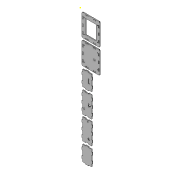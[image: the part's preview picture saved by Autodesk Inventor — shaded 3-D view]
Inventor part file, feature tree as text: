
AUTODESK INVENTOR PART (.ipt)
format: ipt  version: 2022 (Build 260153000, 153)  size: 1,122,816 bytes
history: native  units: mm
features: extrude x6, sketch x1
ambient origin geometry x8: Origin, YZ Plane, XZ Plane, XY Plane, X Axis, Y Axis, Z Axis, Center Point
bodies: Volumenkörper1 (feature_tree), Volumenkörper2 (feature_tree), Volumenkörper3 (feature_tree), Volumenkörper4 (feature_tree), Volumenkörper5 (feature_tree), Volumenkörper6 (feature_tree)
feature tree (7):
  sketch  "Skizze1"  dims[d0=3.0mm d1=0.0mm d2=3.0mm d3=0.0mm d4=3.0mm d5=0.0mm d6=3.0mm d7=0.0mm d8=3.0mm d9=0.0mm d10=3.0mm d11=0.0mm]
  extrude  "Extrusion1"  Depth=3.0mm TaperAngle=0.0deg
  extrude  "Extrusion2"  Depth=3.0mm TaperAngle=0.0deg
  extrude  "Extrusion3"  Depth=3.0mm TaperAngle=0.0deg
  extrude  "Extrusion4"  Depth=3.0mm TaperAngle=0.0deg
  extrude  "Extrusion5"  Depth=3.0mm TaperAngle=0.0deg
  extrude  "Extrusion6"  [1 undecoded]
note: 1 required parameter value undecoded (feature->parameter linkage not recoverable at this tier; creation-order binding heuristic only, values carry confidence <= 0.55)
